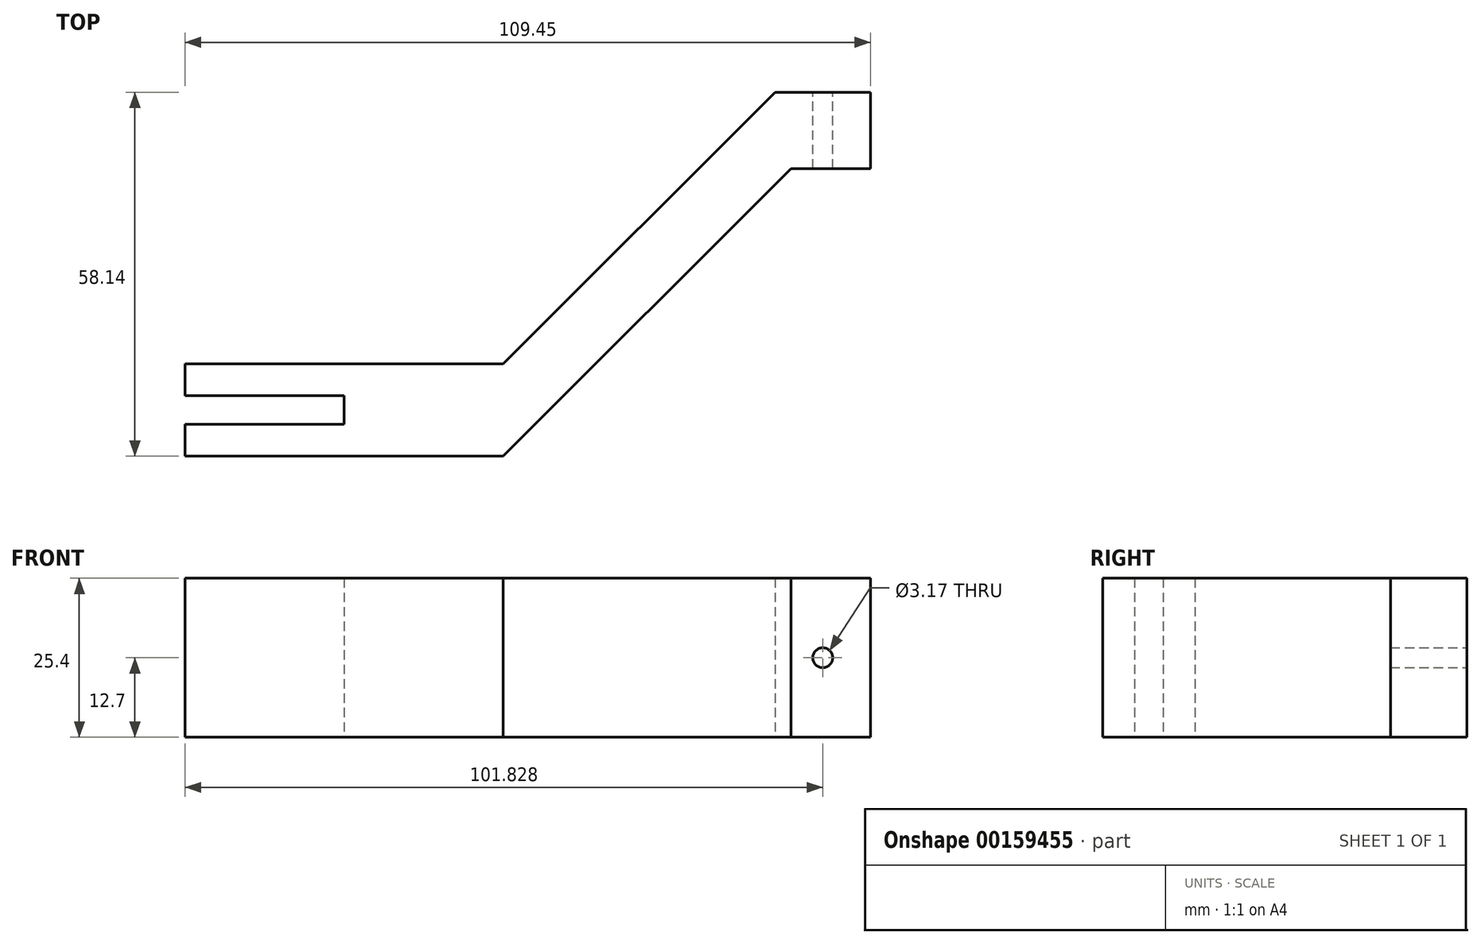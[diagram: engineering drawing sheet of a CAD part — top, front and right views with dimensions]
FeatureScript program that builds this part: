
annotation { "Feature Type Name" : "Feature", "Feature Type Description" : "" }
export const myFeature = defineFeature(function(context is Context, id is Id, definition is map)
    precondition{}
    {
        {
            var Q0;
            Q0=qCreatedBy(makeId("Top.planeOp"),FACE);
            var sketch = newSketch(context, id + "F0", { "sketchPlane" : qUnion([Q0])});
            skLineSegment(sketch, "E0", {"start": v(0, 0) * mm, "end": v(-50.8, 0) * mm});
            skLineSegment(sketch, "E1", {"start": v(-50.8, 0) * mm, "end": v(-50.8, 5.08) * mm});
            skLineSegment(sketch, "E2", {"start": v(-50.8, 5.08) * mm, "end": v(-25.4, 5.08) * mm});
            skLineSegment(sketch, "E3", {"start": v(-25.4, 5.08) * mm, "end": v(-25.4, 9.65) * mm});
            skLineSegment(sketch, "E4", {"start": v(-25.4, 9.65) * mm, "end": v(-50.8, 9.65) * mm});
            skLineSegment(sketch, "E5", {"start": v(-50.8, 9.65) * mm, "end": v(-50.8, 14.73) * mm});
            skLineSegment(sketch, "E6", {"start": v(-50.8, 14.73) * mm, "end": v(0, 14.73) * mm});
            skLineSegment(sketch, "E7", {"start": v(0, 0) * mm, "end": v(45.95, 45.95) * mm});
            skLineSegment(sketch, "E8", {"start": v(45.95, 45.95) * mm, "end": v(58.65, 45.95) * mm});
            skLineSegment(sketch, "E9", {"start": v(58.65, 45.95) * mm, "end": v(58.65, 58.14) * mm});
            skLineSegment(sketch, "E10", {"start": v(0, 14.73) * mm, "end": v(43.4, 58.14) * mm});
            skLineSegment(sketch, "E11", {"start": v(43.4, 58.14) * mm, "end": v(58.65, 58.14) * mm});
            skSolve(sketch);
        }
        {
            var Q0;
            Q0=makeQuery(id+"F0.imprint","IMPRINT",FACE,{"disambiguationData":[TD([[makeQuery(id+"F0.imprint","IMPRINT",EDGE,{"derivedFrom":sQuery(id+"F0.wireOp",EDGE,"E0")}),-1.0]])]});
            extrude(context, id + "F1", {"entities" : qUnion([Q0]), "depth" : 25.4 * mm});
        }
        {
            var Q0;
            Q0=makeQuery(id+"F1.opExtrude","SWEPT_FACE",FACE,{"disambiguationData":[OSD([sQuery(id+"F0.wireOp",EDGE,"E11")])]});
            var sketch = newSketch(context, id + "F2", { "sketchPlane" : qUnion([Q0])});
            skLineSegment(sketch, "E12", {"start": v(-43.4, 25.4) * mm, "end": v(-58.65, 0) * mm, "construction": true});
            skCircle(sketch, "E13", {"center": v(-51.03, 12.7) * mm, "radius": 1.59 * mm});
            skSolve(sketch);
        }
        {
            var Q0;
            Q0=makeQuery(id+"F2.imprint","IMPRINT",FACE,{"disambiguationData":[TD([[makeQuery(id+"F2.imprint","IMPRINT",EDGE,{"derivedFrom":sQuery(id+"F2.wireOp",EDGE,"E13")}),1.0]])]});
            extrude(context, id + "F3", {"entities" : qUnion([Q0]), "operationType" : NewBodyOperationType.REMOVE, "oppositeDirection" : true, "depth" : 25.4 * mm});
        }
    });
